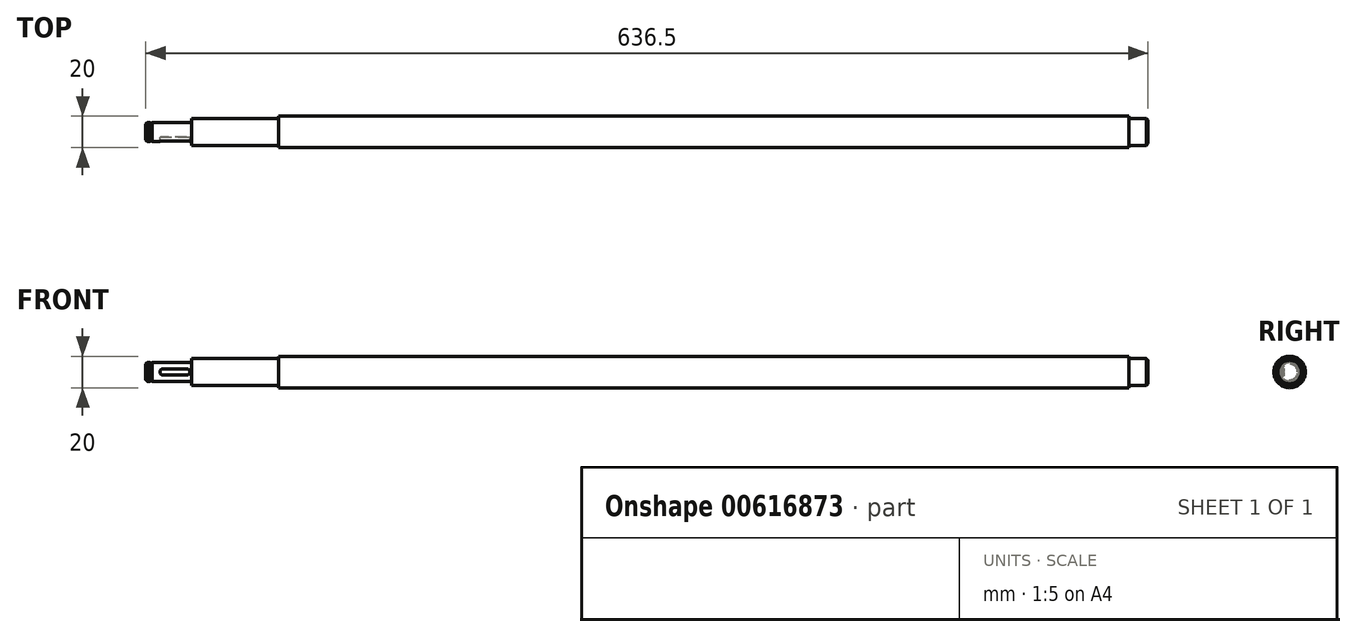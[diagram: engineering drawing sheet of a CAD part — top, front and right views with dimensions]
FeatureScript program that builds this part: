
annotation { "Feature Type Name" : "Feature", "Feature Type Description" : "" }
export const myFeature = defineFeature(function(context is Context, id is Id, definition is map)
    precondition{}
    {
        {
            var Q0;
            Q0=qCreatedBy(makeId("Front.planeOp"),FACE);
            var sketch = newSketch(context, id + "F0", { "sketchPlane" : qUnion([Q0])});
            skLineSegment(sketch, "E0", {"start": v(-291.25, 0) * mm, "end": v(345.25, 0) * mm});
            skLineSegment(sketch, "E1", {"start": v(345.25, 0) * mm, "end": v(345.25, 8.5) * mm});
            skLineSegment(sketch, "E2", {"start": v(345.25, 8.5) * mm, "end": v(333.25, 8.5) * mm});
            skLineSegment(sketch, "E3", {"start": v(333.25, 8.5) * mm, "end": v(333.25, 10) * mm});
            skLineSegment(sketch, "E4", {"start": v(333.25, 10) * mm, "end": v(-206.75, 10) * mm});
            skLineSegment(sketch, "E5", {"start": v(-206.75, 10) * mm, "end": v(-206.75, 8.5) * mm});
            skLineSegment(sketch, "E6", {"start": v(-262.2, 6) * mm, "end": v(-287.2, 6) * mm});
            skLineSegment(sketch, "E7", {"start": v(-291.25, 6) * mm, "end": v(-291.25, 0) * mm});
            skLineSegment(sketch, "E8", {"start": v(-287.2, 6) * mm, "end": v(-287.2, 5.75) * mm});
            skLineSegment(sketch, "E9", {"start": v(-287.2, 5.75) * mm, "end": v(-288.5, 5.75) * mm});
            skLineSegment(sketch, "E10", {"start": v(-288.5, 5.75) * mm, "end": v(-288.5, 6) * mm});
            skLineSegment(sketch, "E11", {"start": v(-288.5, 6) * mm, "end": v(-291.25, 6) * mm});
            skLineSegment(sketch, "E12", {"start": v(-448.42, 0) * mm, "end": v(539.1, 0) * mm, "construction": true});
            skLineSegment(sketch, "E13", {"start": v(-262.2, 6) * mm, "end": v(-262.2, 8.5) * mm});
            skLineSegment(sketch, "E14", {"start": v(-262.2, 8.5) * mm, "end": v(-206.75, 8.5) * mm});
            skSolve(sketch);
        }
        {
            var Q0;
            Q0=qSketchRegion(id+"F0",true);
            var Q1;
            Q1=sQuery(id+"F0.wireOp",EDGE,"E12");
            revolve(context, id + "F1", {"surfaceOperationType" : NewSurfaceOperationType.NEW, "entities" : qUnion([Q0]), "axis" : qUnion([Q1]), "revolveType" : RevolveType.FULL});
        }
        {
            var Q0;
            Q0=makeQuery(id+"F1.opRevolve","SWEPT_EDGE",EDGE,{"disambiguationData":[OSD([sQuery(id+"F0.wireOp",EDGE,"E7"),sQuery(id+"F0.wireOp",EDGE,"E11")])]});
            var Q1;
            Q1=makeQuery(id+"F1.opRevolve","SWEPT_EDGE",EDGE,{"disambiguationData":[OSD([sQuery(id+"F0.wireOp",EDGE,"E1"),sQuery(id+"F0.wireOp",EDGE,"E2")])]});
            chamfer(context, id + "F2", {"entities" : qUnion([Q0, Q1]), "width" : 1 * mm, "tangentPropagation" : true});
        }
        {
            var Q0;
            Q0=qCreatedBy(makeId("Front.planeOp"),FACE);
            var sketch = newSketch(context, id + "F3", { "sketchPlane" : qUnion([Q0])});
            skLineSegment(sketch, "E15.bottom", {"start": v(-280.25, 2) * mm, "end": v(-265.25, 2) * mm});
            skLineSegment(sketch, "E15.top", {"start": v(-280.25, -2) * mm, "end": v(-265.25, -2) * mm});
            skLineSegment(sketch, "E15.left", {"start": v(-280.25, 2) * mm, "end": v(-280.25, -2) * mm});
            skLineSegment(sketch, "E15.right", {"start": v(-265.25, 2) * mm, "end": v(-265.25, -2) * mm});
            skArc(sketch, "E16", {"start": v(-280.25, 2) * mm, "mid": v(-282.25, 0) * mm, "end": v(-280.25, -2) * mm});
            skArc(sketch, "E17", {"start": v(-265.25, -2) * mm, "mid": v(-263.25, 0) * mm, "end": v(-265.25, 2) * mm});
            skLineSegment(sketch, "E18", {"start": v(-341.25, 6) * mm, "end": v(-315.75, 6) * mm, "construction": true});
            skLineSegment(sketch, "E19", {"start": v(-315.75, -6) * mm, "end": v(-341.25, -6) * mm, "construction": true});
            skLineSegment(sketch, "E20", {"start": v(-272.75, 6) * mm, "end": v(-272.75, -6) * mm, "construction": true});
            skSolve(sketch);
        }
        {
            var Q0;
            Q0=qSketchRegion(id+"F3",true);
            var Q1;
            Q1=makeQuery(id+"F1.opRevolve","SWEPT_FACE",FACE,{"disambiguationData":[OSD([sQuery(id+"F0.wireOp",EDGE,"E6")])]});
            extrude(context, id + "F4", {"entities" : qUnion([Q0]), "operationType" : NewBodyOperationType.REMOVE, "depth" : 10 * mm, "offsetDistance" : 2 * mm, "offsetOppositeDirection" : true, "hasSecondDirection" : true, "secondDirectionBound" : BoundingType.UP_TO_SURFACE, "secondDirectionOppositeDirection" : false, "secondDirectionDepth" : 5.3 * mm, "secondDirectionBoundEntityFace" : qUnion([Q1]), "hasSecondDirectionOffset" : true, "secondDirectionOffsetDistance" : 2.5 * mm});
        }
    });
